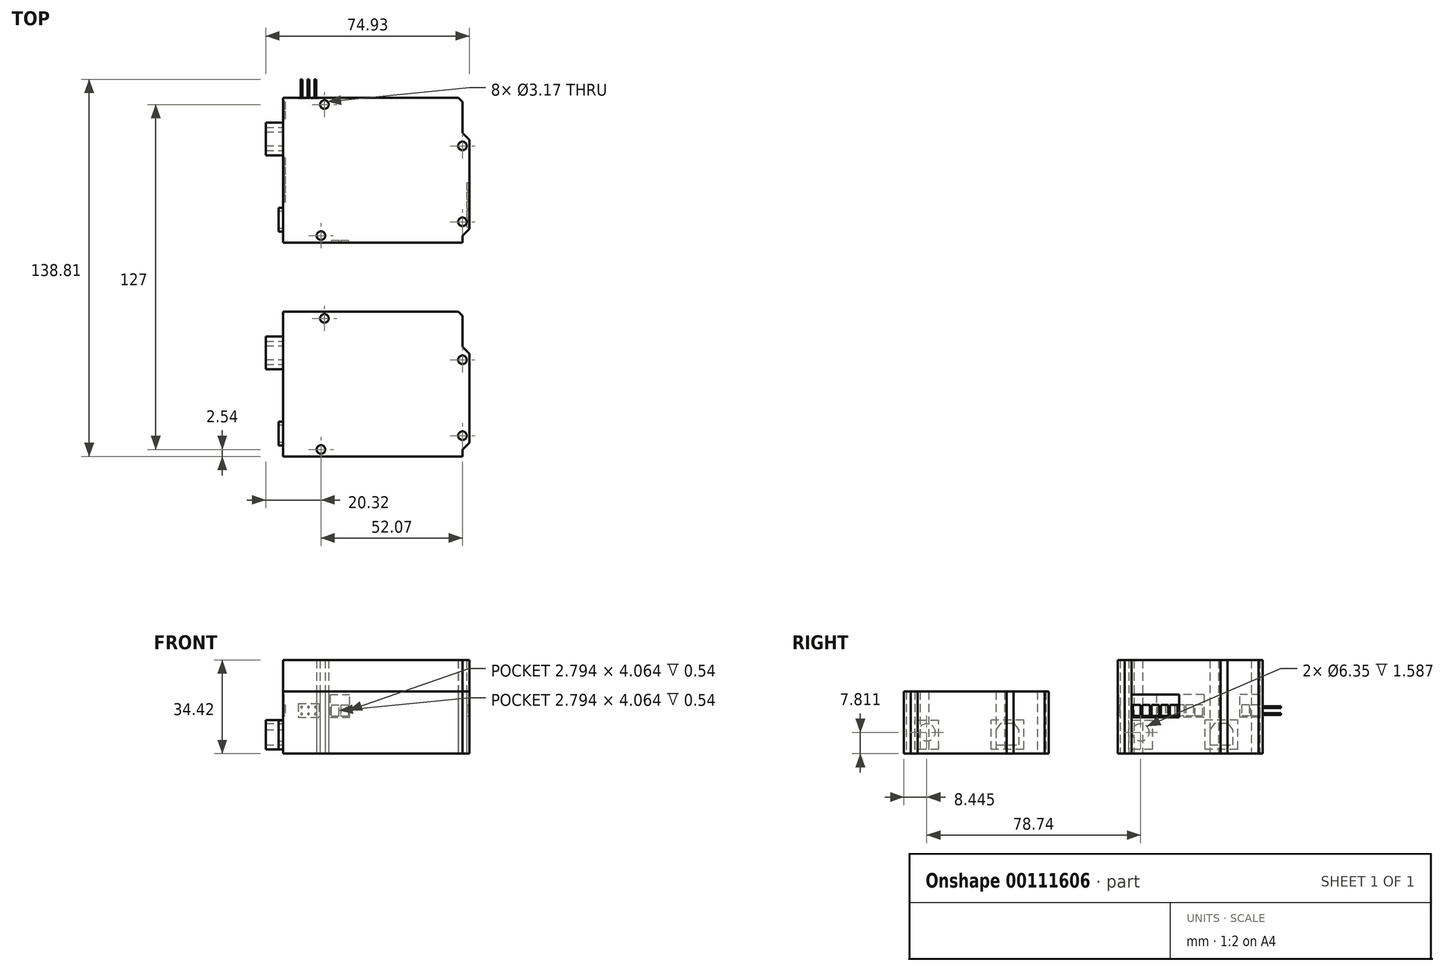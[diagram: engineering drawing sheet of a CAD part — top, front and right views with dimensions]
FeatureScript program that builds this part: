
annotation { "Feature Type Name" : "Feature", "Feature Type Description" : "" }
export const myFeature = defineFeature(function(context is Context, id is Id, definition is map)
    precondition{}
    {
        {
            var Q0;
            Q0=qCreatedBy(makeId("Top.planeOp"),FACE);
            var sketch = newSketch(context, id + "F0", { "sketchPlane" : qUnion([Q0])});
            skLineSegment(sketch, "E0", {"start": v(0, 0) * mm, "end": v(66.04, 0) * mm});
            skLineSegment(sketch, "E1", {"start": v(66.04, 0) * mm, "end": v(66.04, 2.54) * mm});
            skLineSegment(sketch, "E2", {"start": v(66.04, 2.54) * mm, "end": v(68.58, 5.08) * mm});
            skLineSegment(sketch, "E3", {"start": v(68.58, 5.08) * mm, "end": v(68.58, 37.85) * mm});
            skLineSegment(sketch, "E4", {"start": v(68.58, 37.85) * mm, "end": v(66.04, 40.39) * mm});
            skLineSegment(sketch, "E5", {"start": v(66.04, 40.39) * mm, "end": v(66.04, 51.82) * mm});
            skLineSegment(sketch, "E6", {"start": v(66.04, 51.82) * mm, "end": v(64.52, 53.34) * mm});
            skLineSegment(sketch, "E7", {"start": v(64.52, 53.34) * mm, "end": v(0, 53.34) * mm});
            skLineSegment(sketch, "E8", {"start": v(0, 53.34) * mm, "end": v(0, 0) * mm});
            skCircle(sketch, "E9", {"center": v(66.04, 35.56) * mm, "radius": 1.59 * mm});
            skCircle(sketch, "E10", {"center": v(66.04, 7.62) * mm, "radius": 1.59 * mm});
            skCircle(sketch, "E11", {"center": v(13.97, 2.54) * mm, "radius": 1.59 * mm});
            skCircle(sketch, "E12", {"center": v(15.24, 50.8) * mm, "radius": 1.59 * mm});
            skLineSegment(sketch, "E13", {"start": v(0, -78.74) * mm, "end": v(66.04, -78.74) * mm});
            skLineSegment(sketch, "E14", {"start": v(66.04, -78.74) * mm, "end": v(66.04, -76.2) * mm});
            skLineSegment(sketch, "E15", {"start": v(66.04, -76.2) * mm, "end": v(68.58, -73.66) * mm});
            skLineSegment(sketch, "E16", {"start": v(68.58, -73.66) * mm, "end": v(68.58, -40.9) * mm});
            skLineSegment(sketch, "E17", {"start": v(68.58, -40.9) * mm, "end": v(66.04, -38.35) * mm});
            skLineSegment(sketch, "E18", {"start": v(66.04, -38.35) * mm, "end": v(66.04, -26.92) * mm});
            skLineSegment(sketch, "E19", {"start": v(66.04, -26.92) * mm, "end": v(64.52, -25.4) * mm});
            skLineSegment(sketch, "E20", {"start": v(64.52, -25.4) * mm, "end": v(0, -25.4) * mm});
            skLineSegment(sketch, "E21", {"start": v(0, -25.4) * mm, "end": v(0, -78.74) * mm});
            skCircle(sketch, "E22", {"center": v(66.04, -43.18) * mm, "radius": 1.59 * mm});
            skCircle(sketch, "E23", {"center": v(66.04, -71.12) * mm, "radius": 1.59 * mm});
            skCircle(sketch, "E24", {"center": v(13.97, -76.2) * mm, "radius": 1.59 * mm});
            skCircle(sketch, "E25", {"center": v(15.24, -27.94) * mm, "radius": 1.59 * mm});
            skSolve(sketch);
        }
        {
            var Q0;
            Q0=makeQuery(id+"F0.imprint","IMPRINT",FACE,{"disambiguationData":[TD([[makeQuery(id+"F0.imprint","IMPRINT",EDGE,{"derivedFrom":sQuery(id+"F0.wireOp",EDGE,"E0")}),1.0]])]});
            extrude(context, id + "F1", {"entities" : qUnion([Q0]), "depth" : 34.42 * mm});
        }
        {
            var Q0;
            Q0=makeQuery(id+"F0.imprint","IMPRINT",FACE,{"disambiguationData":[TD([[makeQuery(id+"F0.imprint","IMPRINT",EDGE,{"derivedFrom":sQuery(id+"F0.wireOp",EDGE,"E13")}),1.0]])]});
            extrude(context, id + "F2", {"entities" : qUnion([Q0]), "depth" : 22.86 * mm});
        }
        {
            var Q0;
            Q0=makeQuery(id+"F1.opExtrude","SWEPT_FACE",FACE,{"disambiguationData":[OSD([sQuery(id+"F0.wireOp",EDGE,"E3")])]});
            var sketch = newSketch(context, id + "F3", { "sketchPlane" : qUnion([Q0])});
            skLineSegment(sketch, "E26.bottom", {"start": v(5.08, 21.72) * mm, "end": v(22.6, 21.72) * mm});
            skLineSegment(sketch, "E26.top", {"start": v(5.08, 13.34) * mm, "end": v(22.6, 13.34) * mm});
            skLineSegment(sketch, "E26.left", {"start": v(5.08, 21.72) * mm, "end": v(5.08, 13.33) * mm});
            skLineSegment(sketch, "E26.right", {"start": v(22.6, 21.72) * mm, "end": v(22.6, 13.34) * mm});
            skLineSegment(sketch, "E27.bottom", {"start": v(5.64, 13.84) * mm, "end": v(8.43, 13.84) * mm});
            skLineSegment(sketch, "E27.top", {"start": v(5.64, 17.9) * mm, "end": v(8.43, 17.9) * mm});
            skLineSegment(sketch, "E27.left", {"start": v(5.64, 13.84) * mm, "end": v(5.64, 17.9) * mm});
            skLineSegment(sketch, "E27.right", {"start": v(8.43, 13.84) * mm, "end": v(8.43, 17.9) * mm});
            skLineSegment(sketch, "E28.bottom", {"start": v(9.04, 17.9) * mm, "end": v(11.84, 17.9) * mm});
            skLineSegment(sketch, "E28.top", {"start": v(9.04, 13.84) * mm, "end": v(11.84, 13.84) * mm});
            skLineSegment(sketch, "E28.left", {"start": v(9.04, 17.9) * mm, "end": v(9.04, 13.84) * mm});
            skLineSegment(sketch, "E28.right", {"start": v(11.84, 17.9) * mm, "end": v(11.84, 13.84) * mm});
            skLineSegment(sketch, "E29.bottom", {"start": v(12.45, 17.9) * mm, "end": v(15.24, 17.9) * mm});
            skLineSegment(sketch, "E29.top", {"start": v(12.45, 13.84) * mm, "end": v(15.24, 13.84) * mm});
            skLineSegment(sketch, "E29.left", {"start": v(12.45, 17.9) * mm, "end": v(12.45, 13.84) * mm});
            skLineSegment(sketch, "E29.right", {"start": v(15.24, 17.9) * mm, "end": v(15.24, 13.84) * mm});
            skLineSegment(sketch, "E30.bottom", {"start": v(15.85, 17.9) * mm, "end": v(18.64, 17.9) * mm});
            skLineSegment(sketch, "E30.top", {"start": v(15.85, 13.84) * mm, "end": v(18.64, 13.84) * mm});
            skLineSegment(sketch, "E30.left", {"start": v(15.85, 17.9) * mm, "end": v(15.85, 13.84) * mm});
            skLineSegment(sketch, "E30.right", {"start": v(18.64, 17.9) * mm, "end": v(18.64, 13.84) * mm});
            skLineSegment(sketch, "E31.bottom", {"start": v(19.25, 17.9) * mm, "end": v(22.05, 17.9) * mm});
            skLineSegment(sketch, "E31.top", {"start": v(19.25, 13.84) * mm, "end": v(22.05, 13.84) * mm});
            skLineSegment(sketch, "E31.left", {"start": v(19.25, 17.9) * mm, "end": v(19.25, 13.84) * mm});
            skLineSegment(sketch, "E31.right", {"start": v(22.05, 17.9) * mm, "end": v(22.05, 13.84) * mm});
            skSolve(sketch);
        }
        {
            var Q0;
            Q0=makeQuery(id+"F3.imprint","IMPRINT",FACE,{"disambiguationData":[TD([[makeQuery(id+"F3.imprint","IMPRINT",EDGE,{"derivedFrom":sQuery(id+"F3.wireOp",EDGE,"E27.bottom")}),1.0]])]});
            var Q1;
            Q1=makeQuery(id+"F3.imprint","IMPRINT",FACE,{"disambiguationData":[TD([[makeQuery(id+"F3.imprint","IMPRINT",EDGE,{"derivedFrom":sQuery(id+"F3.wireOp",EDGE,"E28.bottom")}),-1.0]])]});
            var Q2;
            Q2=makeQuery(id+"F3.imprint","IMPRINT",FACE,{"disambiguationData":[TD([[makeQuery(id+"F3.imprint","IMPRINT",EDGE,{"derivedFrom":sQuery(id+"F3.wireOp",EDGE,"E29.bottom")}),-1.0]])]});
            var Q3;
            Q3=makeQuery(id+"F3.imprint","IMPRINT",FACE,{"disambiguationData":[TD([[makeQuery(id+"F3.imprint","IMPRINT",EDGE,{"derivedFrom":sQuery(id+"F3.wireOp",EDGE,"E30.bottom")}),-1.0]])]});
            var Q4;
            Q4=makeQuery(id+"F3.imprint","IMPRINT",FACE,{"disambiguationData":[TD([[makeQuery(id+"F3.imprint","IMPRINT",EDGE,{"derivedFrom":sQuery(id+"F3.wireOp",EDGE,"E31.bottom")}),-1.0]])]});
            extrude(context, id + "F4", {"entities" : qUnion([Q0, Q1, Q2, Q3, Q4]), "operationType" : NewBodyOperationType.REMOVE, "oppositeDirection" : true, "depth" : 0.8 * mm});
        }
        {
            var Q0;
            Q0=makeQuery(id+"F3.imprint","IMPRINT",FACE,{"disambiguationData":[TD([[makeQuery(id+"F3.imprint","IMPRINT",EDGE,{"derivedFrom":sQuery(id+"F3.wireOp",EDGE,"E26.bottom")}),-1.0]])]});
            extrude(context, id + "F5", {"entities" : qUnion([Q0]), "operationType" : NewBodyOperationType.REMOVE, "oppositeDirection" : true, "depth" : 0.25 * mm});
        }
        {
            var Q0;
            Q0=makeQuery(id+"F1.opExtrude","SWEPT_FACE",FACE,{"disambiguationData":[OSD([sQuery(id+"F0.wireOp",EDGE,"E8")])]});
            var sketch = newSketch(context, id + "F6", { "sketchPlane" : qUnion([Q0])});
            skLineSegment(sketch, "E32.bottom", {"start": v(-31.75, 21.72) * mm, "end": v(-14.22, 21.72) * mm});
            skLineSegment(sketch, "E32.top", {"start": v(-31.75, 13.33) * mm, "end": v(-14.22, 13.34) * mm});
            skLineSegment(sketch, "E32.left", {"start": v(-31.75, 21.72) * mm, "end": v(-31.75, 13.34) * mm});
            skLineSegment(sketch, "E32.right", {"start": v(-14.22, 21.72) * mm, "end": v(-14.22, 13.34) * mm});
            skLineSegment(sketch, "E33.bottom", {"start": v(-31.2, 13.84) * mm, "end": v(-28.4, 13.84) * mm});
            skLineSegment(sketch, "E33.top", {"start": v(-31.2, 17.9) * mm, "end": v(-28.4, 17.9) * mm});
            skLineSegment(sketch, "E33.left", {"start": v(-31.2, 13.84) * mm, "end": v(-31.2, 17.9) * mm});
            skLineSegment(sketch, "E33.right", {"start": v(-28.4, 13.84) * mm, "end": v(-28.4, 17.9) * mm});
            skLineSegment(sketch, "E34.bottom", {"start": v(-27.79, 17.9) * mm, "end": v(-25, 17.9) * mm});
            skLineSegment(sketch, "E34.top", {"start": v(-27.79, 13.84) * mm, "end": v(-25, 13.84) * mm});
            skLineSegment(sketch, "E34.left", {"start": v(-27.79, 17.9) * mm, "end": v(-27.79, 13.84) * mm});
            skLineSegment(sketch, "E34.right", {"start": v(-25, 17.9) * mm, "end": v(-25, 13.84) * mm});
            skLineSegment(sketch, "E35.bottom", {"start": v(-24.38, 17.9) * mm, "end": v(-21.6, 17.9) * mm});
            skLineSegment(sketch, "E35.top", {"start": v(-24.38, 13.84) * mm, "end": v(-21.59, 13.84) * mm});
            skLineSegment(sketch, "E35.left", {"start": v(-24.38, 17.9) * mm, "end": v(-24.38, 13.84) * mm});
            skLineSegment(sketch, "E35.right", {"start": v(-21.59, 17.9) * mm, "end": v(-21.59, 13.84) * mm});
            skLineSegment(sketch, "E36.bottom", {"start": v(-20.98, 17.9) * mm, "end": v(-18.19, 17.9) * mm});
            skLineSegment(sketch, "E36.top", {"start": v(-20.98, 13.84) * mm, "end": v(-18.19, 13.84) * mm});
            skLineSegment(sketch, "E36.left", {"start": v(-20.98, 17.9) * mm, "end": v(-20.98, 13.84) * mm});
            skLineSegment(sketch, "E36.right", {"start": v(-18.19, 17.9) * mm, "end": v(-18.19, 13.84) * mm});
            skLineSegment(sketch, "E37.bottom", {"start": v(-17.58, 17.9) * mm, "end": v(-14.78, 17.9) * mm});
            skLineSegment(sketch, "E37.top", {"start": v(-17.58, 13.84) * mm, "end": v(-14.78, 13.84) * mm});
            skLineSegment(sketch, "E37.left", {"start": v(-17.58, 17.9) * mm, "end": v(-17.58, 13.84) * mm});
            skLineSegment(sketch, "E37.right", {"start": v(-14.78, 17.9) * mm, "end": v(-14.78, 13.84) * mm});
            skLineSegment(sketch, "E38.0", {"start": v(-5.08, 13.34) * mm, "end": v(-22.6, 13.34) * mm});
            skLineSegment(sketch, "E39", {"start": v(-24.38, 17.9) * mm, "end": v(-24.38, 21.72) * mm});
            skLineSegment(sketch, "E40", {"start": v(-24.38, 13.84) * mm, "end": v(-24.38, 13.34) * mm});
            skLineSegment(sketch, "E41.bottom", {"start": v(-52.32, 21.72) * mm, "end": v(-45, 21.72) * mm});
            skLineSegment(sketch, "E41.top", {"start": v(-52.32, 13.33) * mm, "end": v(-45, 13.33) * mm});
            skLineSegment(sketch, "E41.left", {"start": v(-52.32, 21.72) * mm, "end": v(-52.32, 13.33) * mm});
            skLineSegment(sketch, "E42.bottom", {"start": v(-51.77, 13.84) * mm, "end": v(-48.97, 13.84) * mm});
            skLineSegment(sketch, "E42.top", {"start": v(-51.77, 17.9) * mm, "end": v(-48.97, 17.9) * mm});
            skLineSegment(sketch, "E42.left", {"start": v(-51.77, 13.84) * mm, "end": v(-51.77, 17.9) * mm});
            skLineSegment(sketch, "E42.right", {"start": v(-48.97, 13.84) * mm, "end": v(-48.97, 17.9) * mm});
            skLineSegment(sketch, "E43.bottom", {"start": v(-48.36, 17.9) * mm, "end": v(-45.57, 17.9) * mm});
            skLineSegment(sketch, "E43.top", {"start": v(-48.36, 13.84) * mm, "end": v(-45.57, 13.84) * mm});
            skLineSegment(sketch, "E43.left", {"start": v(-48.36, 17.9) * mm, "end": v(-48.36, 13.84) * mm});
            skLineSegment(sketch, "E43.right", {"start": v(-45.57, 17.9) * mm, "end": v(-45.57, 13.84) * mm});
            skLineSegment(sketch, "E44", {"start": v(-45, 13.33) * mm, "end": v(-45, 21.72) * mm});
            skLineSegment(sketch, "E45.bottom", {"start": v(-44.2, 1.59) * mm, "end": v(-32.13, 1.59) * mm});
            skLineSegment(sketch, "E45.top", {"start": v(-44.2, 12.38) * mm, "end": v(-32.13, 12.38) * mm});
            skLineSegment(sketch, "E45.left", {"start": v(-44.2, 1.59) * mm, "end": v(-44.2, 12.38) * mm});
            skLineSegment(sketch, "E45.right", {"start": v(-32.13, 1.59) * mm, "end": v(-32.13, 12.38) * mm});
            skLineSegment(sketch, "E46.bottom", {"start": v(-12.83, 1.59) * mm, "end": v(-4.06, 1.59) * mm});
            skLineSegment(sketch, "E46.top", {"start": v(-12.83, 12.26) * mm, "end": v(-4.06, 12.26) * mm});
            skLineSegment(sketch, "E46.left", {"start": v(-12.83, 1.59) * mm, "end": v(-12.83, 12.26) * mm});
            skLineSegment(sketch, "E46.right", {"start": v(-4.06, 1.59) * mm, "end": v(-4.06, 12.26) * mm});
            skCircle(sketch, "E47", {"center": v(-8.45, 7.81) * mm, "radius": 3.18 * mm});
            skPoint(sketch, "E48", {"position": v(-8.45, 12.26) * mm});
            skLineSegment(sketch, "E49", {"start": v(-42.42, 3.17) * mm, "end": v(-42.42, 8.72) * mm});
            skLineSegment(sketch, "E50", {"start": v(-42.42, 8.72) * mm, "end": v(-40.7, 11.01) * mm});
            skLineSegment(sketch, "E51", {"start": v(-40.7, 11.01) * mm, "end": v(-35.62, 11.01) * mm});
            skLineSegment(sketch, "E52", {"start": v(-35.62, 11.01) * mm, "end": v(-33.9, 8.72) * mm});
            skLineSegment(sketch, "E53", {"start": v(-33.9, 8.72) * mm, "end": v(-33.9, 3.17) * mm});
            skLineSegment(sketch, "E54", {"start": v(-33.9, 3.18) * mm, "end": v(-42.42, 3.17) * mm});
            skPoint(sketch, "E55", {"position": v(-38.16, 11.01) * mm});
            skPoint(sketch, "E56", {"position": v(-38.16, 3.18) * mm});
            skPoint(sketch, "E57", {"position": v(-38.16, 12.38) * mm});
            skLineSegment(sketch, "E58.bottom", {"start": v(34.54, 1.59) * mm, "end": v(46.6, 1.59) * mm});
            skLineSegment(sketch, "E58.top", {"start": v(34.54, 12.38) * mm, "end": v(46.6, 12.38) * mm});
            skLineSegment(sketch, "E58.left", {"start": v(34.54, 1.59) * mm, "end": v(34.54, 12.38) * mm});
            skLineSegment(sketch, "E58.right", {"start": v(46.6, 1.59) * mm, "end": v(46.6, 12.38) * mm});
            skLineSegment(sketch, "E59.bottom", {"start": v(65.91, 1.59) * mm, "end": v(74.68, 1.59) * mm});
            skLineSegment(sketch, "E59.top", {"start": v(65.91, 12.26) * mm, "end": v(74.68, 12.26) * mm});
            skLineSegment(sketch, "E59.left", {"start": v(65.91, 1.59) * mm, "end": v(65.91, 12.26) * mm});
            skLineSegment(sketch, "E59.right", {"start": v(74.68, 1.59) * mm, "end": v(74.68, 12.26) * mm});
            skCircle(sketch, "E60", {"center": v(70.3, 7.81) * mm, "radius": 3.18 * mm});
            skPoint(sketch, "E61", {"position": v(70.3, 12.26) * mm});
            skLineSegment(sketch, "E62", {"start": v(36.32, 3.18) * mm, "end": v(36.32, 8.72) * mm});
            skLineSegment(sketch, "E63", {"start": v(36.32, 8.72) * mm, "end": v(38.04, 11.01) * mm});
            skLineSegment(sketch, "E64", {"start": v(38.04, 11.01) * mm, "end": v(43.12, 11.01) * mm});
            skLineSegment(sketch, "E65", {"start": v(43.12, 11.01) * mm, "end": v(44.83, 8.72) * mm});
            skLineSegment(sketch, "E66", {"start": v(44.83, 8.72) * mm, "end": v(44.83, 3.18) * mm});
            skLineSegment(sketch, "E67", {"start": v(44.83, 3.17) * mm, "end": v(36.32, 3.17) * mm});
            skPoint(sketch, "E68", {"position": v(40.58, 11.01) * mm});
            skPoint(sketch, "E69", {"position": v(40.58, 3.18) * mm});
            skPoint(sketch, "E70", {"position": v(40.58, 12.38) * mm});
            skSolve(sketch);
        }
        {
            var Q0;
            Q0=makeQuery(id+"F6.imprint","IMPRINT",FACE,{"disambiguationData":[TD([[makeQuery(id+"F6.imprint","IMPRINT",EDGE,{"derivedFrom":sQuery(id+"F6.wireOp",EDGE,"E43.bottom")}),-1.0]])]});
            var Q1;
            Q1=makeQuery(id+"F6.imprint","IMPRINT",FACE,{"disambiguationData":[TD([[makeQuery(id+"F6.imprint","IMPRINT",EDGE,{"derivedFrom":sQuery(id+"F6.wireOp",EDGE,"E33.bottom")}),1.0]])]});
            var Q2;
            Q2=makeQuery(id+"F6.imprint","IMPRINT",FACE,{"disambiguationData":[TD([[makeQuery(id+"F6.imprint","IMPRINT",EDGE,{"derivedFrom":sQuery(id+"F6.wireOp",EDGE,"E34.bottom")}),-1.0]])]});
            var Q3;
            Q3=makeQuery(id+"F6.imprint","IMPRINT",FACE,{"disambiguationData":[TD([[makeQuery(id+"F6.imprint","IMPRINT",EDGE,{"derivedFrom":sQuery(id+"F6.wireOp",EDGE,"E35.bottom")}),-1.0]])]});
            var Q4;
            Q4=makeQuery(id+"F6.imprint","IMPRINT",FACE,{"disambiguationData":[TD([[makeQuery(id+"F6.imprint","IMPRINT",EDGE,{"derivedFrom":sQuery(id+"F6.wireOp",EDGE,"E36.bottom")}),-1.0]])]});
            var Q5;
            Q5=makeQuery(id+"F6.imprint","IMPRINT",FACE,{"disambiguationData":[TD([[makeQuery(id+"F6.imprint","IMPRINT",EDGE,{"derivedFrom":sQuery(id+"F6.wireOp",EDGE,"E37.bottom")}),-1.0]])]});
            var Q6;
            Q6=makeQuery(id+"F6.imprint","IMPRINT",FACE,{"disambiguationData":[TD([[makeQuery(id+"F6.imprint","IMPRINT",EDGE,{"derivedFrom":sQuery(id+"F6.wireOp",EDGE,"E42.bottom")}),1.0]])]});
            var Q7;
            Q7=sQuery(id+"F6.wireOp",EDGE,"E42.top");
            extrude(context, id + "F7", {"entities" : qUnion([Q0, Q1, Q2, Q3, Q4, Q5, Q6]), "operationType" : NewBodyOperationType.REMOVE, "surfaceEntities" : qUnion([Q7]), "oppositeDirection" : true, "depth" : 0.8 * mm});
        }
        {
            var Q0;
            Q0=makeQuery(id+"F6.imprint","IMPRINT",FACE,{"disambiguationData":[TD([[makeQuery(id+"F6.imprint","IMPRINT",EDGE,{"derivedFrom":sQuery(id+"F6.wireOp",EDGE,"E41.bottom")}),-1.0]])]});
            var Q1;
            {var subQ0=sQuery(id+"F6.wireOp",EDGE,"E32.left");Q1=makeQuery(id+"F6.imprint","IMPRINT",FACE,{"disambiguationData":[TD([[makeQuery(id+"F6.imprint","IMPRINT",EDGE,{"derivedFrom":subQ0}),1.0]])]});}
            var Q2;
            {var subQ0=sQuery(id+"F6.wireOp",EDGE,"E32.right");Q2=makeQuery(id+"F6.imprint","IMPRINT",FACE,{"disambiguationData":[TD([[makeQuery(id+"F6.imprint","IMPRINT",EDGE,{"derivedFrom":subQ0}),-1.0]])]});}
            extrude(context, id + "F8", {"entities" : qUnion([Q0, Q1, Q2]), "operationType" : NewBodyOperationType.REMOVE, "oppositeDirection" : true, "depth" : 0.25 * mm});
        }
        {
            var Q0;
            Q0=makeQuery(id+"F1.opExtrude","SWEPT_FACE",FACE,{"disambiguationData":[OSD([sQuery(id+"F0.wireOp",EDGE,"E0")])]});
            var sketch = newSketch(context, id + "F9", { "sketchPlane" : qUnion([Q0])});
            skPoint(sketch, "E71.0", {"position": v(0, 13.34) * mm});
            skLineSegment(sketch, "E72.bottom", {"start": v(17.27, 21.72) * mm, "end": v(24.59, 21.72) * mm});
            skLineSegment(sketch, "E72.top", {"start": v(17.27, 13.34) * mm, "end": v(24.59, 13.34) * mm});
            skLineSegment(sketch, "E72.left", {"start": v(17.27, 21.72) * mm, "end": v(17.27, 13.33) * mm});
            skLineSegment(sketch, "E73.bottom", {"start": v(17.83, 13.84) * mm, "end": v(20.62, 13.84) * mm});
            skLineSegment(sketch, "E73.top", {"start": v(17.83, 17.9) * mm, "end": v(20.62, 17.9) * mm});
            skLineSegment(sketch, "E73.left", {"start": v(17.83, 13.84) * mm, "end": v(17.83, 17.9) * mm});
            skLineSegment(sketch, "E73.right", {"start": v(20.62, 13.84) * mm, "end": v(20.62, 17.9) * mm});
            skLineSegment(sketch, "E74.bottom", {"start": v(21.23, 17.9) * mm, "end": v(24.03, 17.9) * mm});
            skLineSegment(sketch, "E74.top", {"start": v(21.23, 13.84) * mm, "end": v(24.03, 13.84) * mm});
            skLineSegment(sketch, "E74.left", {"start": v(21.23, 17.9) * mm, "end": v(21.23, 13.84) * mm});
            skLineSegment(sketch, "E74.right", {"start": v(24.03, 17.9) * mm, "end": v(24.03, 13.84) * mm});
            skLineSegment(sketch, "E75", {"start": v(24.59, 13.34) * mm, "end": v(24.59, 21.72) * mm});
            skPoint(sketch, "E76.0", {"position": v(0, 21.72) * mm});
            skSolve(sketch);
        }
        {
            var Q0;
            Q0=makeQuery(id+"F9.imprint","IMPRINT",FACE,{"disambiguationData":[TD([[makeQuery(id+"F9.imprint","IMPRINT",EDGE,{"derivedFrom":sQuery(id+"F9.wireOp",EDGE,"E72.bottom")}),-1.0]])]});
            extrude(context, id + "F10", {"entities" : qUnion([Q0]), "operationType" : NewBodyOperationType.REMOVE, "oppositeDirection" : true, "depth" : 0.25 * mm});
        }
        {
            var Q0;
            Q0=makeQuery(id+"F10.boolean.opBoolean","SPLIT",FACE,{"disambiguationData":[TD([makeQuery(id+"F10.opExtrude","SWEPT_FACE",FACE,{"disambiguationData":[OSD([sQuery(id+"F9.wireOp",EDGE,"E73.bottom")])]})])],"derivedFrom":makeQuery(id+"F1.opExtrude","SWEPT_FACE",FACE,{"disambiguationData":[OSD([sQuery(id+"F0.wireOp",EDGE,"E0")])]})});
            var Q1;
            Q1=makeQuery(id+"F10.boolean.opBoolean","SPLIT",FACE,{"disambiguationData":[TD([makeQuery(id+"F10.opExtrude","SWEPT_FACE",FACE,{"disambiguationData":[OSD([sQuery(id+"F9.wireOp",EDGE,"E74.bottom")])]})])],"derivedFrom":makeQuery(id+"F1.opExtrude","SWEPT_FACE",FACE,{"disambiguationData":[OSD([sQuery(id+"F0.wireOp",EDGE,"E0")])]})});
            extrude(context, id + "F11", {"entities" : qUnion([Q0, Q1]), "operationType" : NewBodyOperationType.REMOVE, "oppositeDirection" : true, "depth" : 0.8 * mm});
        }
        {
            var Q0;
            Q0=makeQuery(id+"F1.opExtrude","SWEPT_FACE",FACE,{"disambiguationData":[OSD([sQuery(id+"F0.wireOp",EDGE,"E7")])]});
            var sketch = newSketch(context, id + "F12", { "sketchPlane" : qUnion([Q0])});
            skLineSegment(sketch, "E77.bottom", {"start": v(-5.59, 18.41) * mm, "end": v(-13.2, 18.41) * mm});
            skLineSegment(sketch, "E77.top", {"start": v(-5.59, 13.33) * mm, "end": v(-13.2, 13.33) * mm});
            skLineSegment(sketch, "E77.left", {"start": v(-5.59, 18.41) * mm, "end": v(-5.59, 13.33) * mm});
            skLineSegment(sketch, "E77.right", {"start": v(-13.2, 18.41) * mm, "end": v(-13.2, 13.33) * mm});
            skPoint(sketch, "E78.0", {"position": v(0, 13.33) * mm});
            skCircle(sketch, "E79", {"center": v(-11.94, 17.14) * mm, "radius": 0.32 * mm});
            skCircle(sketch, "E80.0.1.0", {"center": v(-11.94, 14.6) * mm, "radius": 0.32 * mm});
            skCircle(sketch, "E80.1.0.0", {"center": v(-9.4, 17.14) * mm, "radius": 0.32 * mm});
            skCircle(sketch, "E80.1.1.0", {"center": v(-9.4, 14.6) * mm, "radius": 0.32 * mm});
            skCircle(sketch, "E80.2.0.0", {"center": v(-6.86, 17.14) * mm, "radius": 0.32 * mm});
            skCircle(sketch, "E80.2.1.0", {"center": v(-6.86, 14.6) * mm, "radius": 0.32 * mm});
            skLineSegment(sketch, "E80.direction1", {"start": v(-11.94, 17.14) * mm, "end": v(-9.4, 17.14) * mm, "construction": true});
            skLineSegment(sketch, "E80.direction2", {"start": v(-11.94, 17.14) * mm, "end": v(-11.94, 14.6) * mm, "construction": true});
            skSolve(sketch);
        }
        {
            var Q0;
            Q0=makeQuery(id+"F12.imprint","IMPRINT",FACE,{"disambiguationData":[TD([[makeQuery(id+"F12.imprint","IMPRINT",EDGE,{"derivedFrom":sQuery(id+"F12.wireOp",EDGE,"E77.bottom")}),1.0]])]});
            extrude(context, id + "F13", {"entities" : qUnion([Q0]), "operationType" : NewBodyOperationType.REMOVE, "oppositeDirection" : true, "depth" : 0.25 * mm});
        }
        {
            var Q0;
            Q0=makeQuery(id+"F13.boolean.opBoolean","SPLIT",FACE,{"disambiguationData":[TD([makeQuery(id+"F13.opExtrude","SWEPT_FACE",FACE,{"disambiguationData":[OSD([sQuery(id+"F12.wireOp",EDGE,"E80.1.0.0")])]})])],"derivedFrom":makeQuery(id+"F1.opExtrude","SWEPT_FACE",FACE,{"disambiguationData":[OSD([sQuery(id+"F0.wireOp",EDGE,"E7")])]})});
            var Q1;
            Q1=makeQuery(id+"F13.boolean.opBoolean","SPLIT",FACE,{"disambiguationData":[TD([makeQuery(id+"F13.opExtrude","SWEPT_FACE",FACE,{"disambiguationData":[OSD([sQuery(id+"F12.wireOp",EDGE,"E80.2.0.0")])]})])],"derivedFrom":makeQuery(id+"F1.opExtrude","SWEPT_FACE",FACE,{"disambiguationData":[OSD([sQuery(id+"F0.wireOp",EDGE,"E7")])]})});
            var Q2;
            Q2=makeQuery(id+"F13.boolean.opBoolean","SPLIT",FACE,{"disambiguationData":[TD([makeQuery(id+"F13.opExtrude","SWEPT_FACE",FACE,{"disambiguationData":[OSD([sQuery(id+"F12.wireOp",EDGE,"E79")])]})])],"derivedFrom":makeQuery(id+"F1.opExtrude","SWEPT_FACE",FACE,{"disambiguationData":[OSD([sQuery(id+"F0.wireOp",EDGE,"E7")])]})});
            var Q3;
            Q3=makeQuery(id+"F13.boolean.opBoolean","SPLIT",FACE,{"disambiguationData":[TD([makeQuery(id+"F13.opExtrude","SWEPT_FACE",FACE,{"disambiguationData":[OSD([sQuery(id+"F12.wireOp",EDGE,"E80.0.1.0")])]})])],"derivedFrom":makeQuery(id+"F1.opExtrude","SWEPT_FACE",FACE,{"disambiguationData":[OSD([sQuery(id+"F0.wireOp",EDGE,"E7")])]})});
            var Q4;
            Q4=makeQuery(id+"F13.boolean.opBoolean","SPLIT",FACE,{"disambiguationData":[TD([makeQuery(id+"F13.opExtrude","SWEPT_FACE",FACE,{"disambiguationData":[OSD([sQuery(id+"F12.wireOp",EDGE,"E80.1.1.0")])]})])],"derivedFrom":makeQuery(id+"F1.opExtrude","SWEPT_FACE",FACE,{"disambiguationData":[OSD([sQuery(id+"F0.wireOp",EDGE,"E7")])]})});
            var Q5;
            Q5=makeQuery(id+"F13.boolean.opBoolean","SPLIT",FACE,{"disambiguationData":[TD([makeQuery(id+"F13.opExtrude","SWEPT_FACE",FACE,{"disambiguationData":[OSD([sQuery(id+"F12.wireOp",EDGE,"E80.2.1.0")])]})])],"derivedFrom":makeQuery(id+"F1.opExtrude","SWEPT_FACE",FACE,{"disambiguationData":[OSD([sQuery(id+"F0.wireOp",EDGE,"E7")])]})});
            extrude(context, id + "F14", {"entities" : qUnion([Q0, Q1, Q2, Q3, Q4, Q5]), "operationType" : NewBodyOperationType.ADD, "depth" : 6.73 * mm});
        }
        {
            var Q0;
            Q0=makeQuery(id+"F6.imprint","IMPRINT",FACE,{"disambiguationData":[TD([[makeQuery(id+"F6.imprint","IMPRINT",EDGE,{"derivedFrom":sQuery(id+"F6.wireOp",EDGE,"E45.bottom")}),1.0]])]});
            var Q1;
            Q1=makeQuery(id+"F6.imprint","IMPRINT",FACE,{"disambiguationData":[TD([[makeQuery(id+"F6.imprint","IMPRINT",EDGE,{"derivedFrom":sQuery(id+"F6.wireOp",EDGE,"E58.bottom")}),1.0]])]});
            extrude(context, id + "F15", {"entities" : qUnion([Q0, Q1]), "operationType" : NewBodyOperationType.ADD, "depth" : 6.35 * mm});
        }
        {
            var Q0;
            Q0=makeQuery(id+"F6.imprint","IMPRINT",FACE,{"disambiguationData":[TD([[makeQuery(id+"F6.imprint","IMPRINT",EDGE,{"derivedFrom":sQuery(id+"F6.wireOp",EDGE,"E46.bottom")}),1.0]])]});
            var Q1;
            Q1=makeQuery(id+"F6.imprint","IMPRINT",FACE,{"disambiguationData":[TD([[makeQuery(id+"F6.imprint","IMPRINT",EDGE,{"derivedFrom":sQuery(id+"F6.wireOp",EDGE,"E59.bottom")}),1.0]])]});
            extrude(context, id + "F16", {"entities" : qUnion([Q0, Q1]), "operationType" : NewBodyOperationType.ADD, "depth" : 1.59 * mm});
        }
    });
